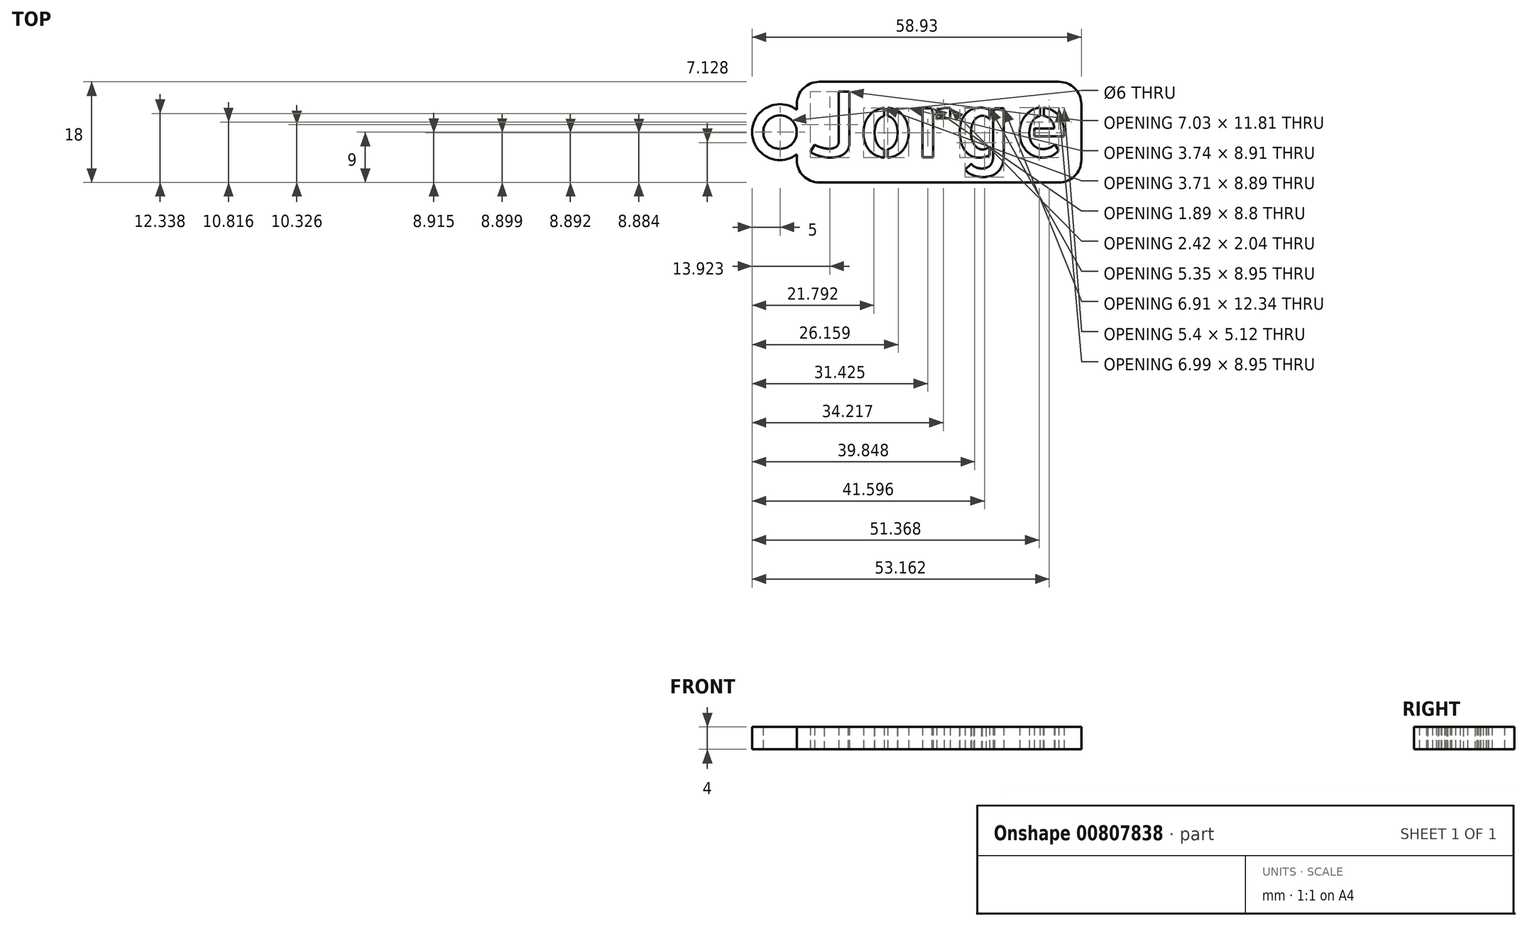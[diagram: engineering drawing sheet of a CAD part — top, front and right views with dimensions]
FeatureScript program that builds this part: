
annotation { "Feature Type Name" : "Feature", "Feature Type Description" : "" }
export const myFeature = defineFeature(function(context is Context, id is Id, definition is map)
    precondition{}
    {
        {
            var Q0;
            Q0=qCreatedBy(makeId("Top.planeOp"),FACE);
            var sketch = newSketch(context, id + "F0", { "sketchPlane" : qUnion([Q0])});
            skLineSegment(sketch, "E0.bottom", {"start": v(-2, -4.5) * mm, "end": v(48.93, -4.5) * mm});
            skLineSegment(sketch, "E0.top", {"start": v(-2, 13.5) * mm, "end": v(48.93, 13.5) * mm});
            skLineSegment(sketch, "E0.left", {"start": v(-2, -4.5) * mm, "end": v(-2, 0.5) * mm});
            skLineSegment(sketch, "E0.right", {"start": v(48.93, -4.5) * mm, "end": v(48.93, 13.5) * mm});
            skArc(sketch, "E1", {"start": v(-2, 8.5) * mm, "mid": v(-10, 4.5) * mm, "end": v(-2, 0.5) * mm});
            skLineSegment(sketch, "E2.trimOffspring", {"start": v(-2, 8.5) * mm, "end": v(-2, 13.5) * mm});
            skCircle(sketch, "E3", {"center": v(-5, 4.5) * mm, "radius": 3 * mm});
            skLineSegment(sketch, "E4", {"start": v(48.93, 4.5) * mm, "end": v(-10, 4.5) * mm, "construction": true});
            skText(sketch, "E5", { "text": "Jorge", "fontName": "AllertaStencil-Regular.ttf"});
            const initialGuessF0  = {"E5": [0, 0, 1, 0, 0.0115]};
            skSetInitialGuess(sketch, initialGuessF0);
            skSolve(sketch);
        }
        {
            var Q0;
            Q0=makeQuery(id+"F0.imprint","IMPRINT",FACE,{"disambiguationData":[TD([[makeQuery(id+"F0.imprint","IMPRINT",EDGE,{"derivedFrom":sQuery(id+"F0.wireOp",EDGE,"E0.bottom")}),1.0]])]});
            extrude(context, id + "F1", {"entities" : qUnion([Q0]), "depth" : 4 * mm, "offsetDistance" : 25 * mm});
        }
        {
            var Q0;
            Q0=makeQuery(id+"F1.opExtrude","SWEPT_EDGE",EDGE,{"disambiguationData":[OSD([sQuery(id+"F0.wireOp",EDGE,"E0.bottom"),sQuery(id+"F0.wireOp",EDGE,"E0.left")])]});
            var Q1;
            Q1=makeQuery(id+"F1.opExtrude","SWEPT_EDGE",EDGE,{"disambiguationData":[OSD([sQuery(id+"F0.wireOp",EDGE,"E0.bottom"),sQuery(id+"F0.wireOp",EDGE,"E0.right")])]});
            var Q2;
            Q2=makeQuery(id+"F1.opExtrude","SWEPT_EDGE",EDGE,{"disambiguationData":[OSD([sQuery(id+"F0.wireOp",EDGE,"E0.top"),sQuery(id+"F0.wireOp",EDGE,"E0.right")])]});
            var Q3;
            Q3=makeQuery(id+"F1.opExtrude","SWEPT_EDGE",EDGE,{"disambiguationData":[OSD([sQuery(id+"F0.wireOp",EDGE,"E0.top"),sQuery(id+"F0.wireOp",EDGE,"E2.trimOffspring")])]});
            fillet(context, id + "F2", {"entities" : qUnion([Q0, Q1, Q2, Q3]), "radius" : 4 * mm, "tangentPropagation" : true, "allowEdgeOverflow" : false});
        }
    });
